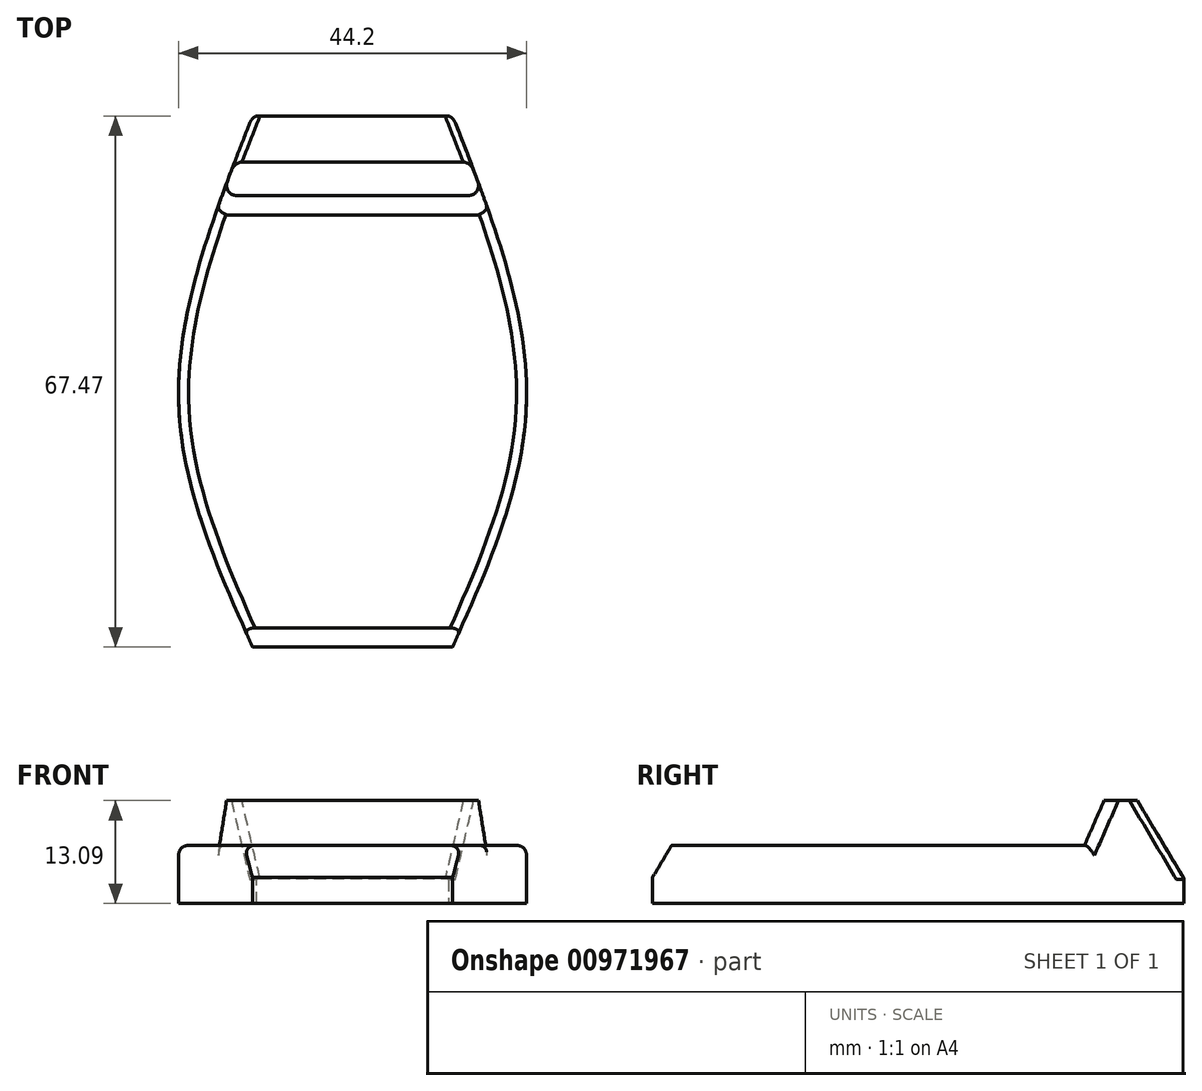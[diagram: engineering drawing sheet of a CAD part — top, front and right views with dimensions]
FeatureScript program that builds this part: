
annotation { "Feature Type Name" : "Feature", "Feature Type Description" : "" }
export const myFeature = defineFeature(function(context is Context, id is Id, definition is map)
    precondition{}
    {
        {
            var Q0;
            Q0=qCreatedBy(makeId("Right.planeOp"),FACE);
            var sketch = newSketch(context, id + "F0", { "sketchPlane" : qUnion([Q0])});
            skLineSegment(sketch, "E0", {"start": v(-30.67, 0) * mm, "end": v(37.07, 0) * mm});
            skLineSegment(sketch, "E1", {"start": v(-17.97, 4.35) * mm, "end": v(24.37, 4.35) * mm});
            skLineSegment(sketch, "E2", {"start": v(37.07, 0) * mm, "end": v(31.1, 10.04) * mm});
            skLineSegment(sketch, "E3", {"start": v(31.1, 10.04) * mm, "end": v(26.86, 10.04) * mm});
            skLineSegment(sketch, "E4", {"start": v(26.86, 10.04) * mm, "end": v(24.37, 4.35) * mm});
            skLineSegment(sketch, "E5", {"start": v(3.2, 0) * mm, "end": v(3.2, 4.35) * mm});
            skLineSegment(sketch, "E6.bottom", {"start": v(-67.15, 50) * mm, "end": v(95.4, 50) * mm});
            skLineSegment(sketch, "E6.top", {"start": v(-67.15, -41.02) * mm, "end": v(95.4, -41.02) * mm});
            skLineSegment(sketch, "E6.left", {"start": v(-67.15, 50) * mm, "end": v(-67.15, -41.02) * mm});
            skLineSegment(sketch, "E6.right", {"start": v(95.4, 50) * mm, "end": v(95.4, -41.02) * mm});
            skLineSegment(sketch, "E7", {"start": v(-17.97, 4.35) * mm, "end": v(-28.07, 4.35) * mm});
            skLineSegment(sketch, "E8", {"start": v(-28.07, 4.35) * mm, "end": v(-30.67, 0) * mm});
            skSolve(sketch);
        }
        {
            var Q0;
            Q0=qCreatedBy(makeId("Top.planeOp"),FACE);
            var sketch = newSketch(context, id + "F1", { "sketchPlane" : qUnion([Q0])});
            skLineSegment(sketch, "E9", {"start": v(0, 11.41) * mm, "end": v(0, -9.41) * mm});
            skLineSegment(sketch, "E10", {"start": v(0, 1) * mm, "end": v(-22.1, 1) * mm});
            skLineSegment(sketch, "E11", {"start": v(0, 1) * mm, "end": v(0, -30.51) * mm});
            skLineSegment(sketch, "E12", {"start": v(0, -30.51) * mm, "end": v(0, 36.96) * mm});
            skLineSegment(sketch, "E13", {"start": v(0, 36.96) * mm, "end": v(-12.7, 36.96) * mm});
            skLineSegment(sketch, "E14", {"start": v(0, 36.96) * mm, "end": v(12.7, 36.96) * mm});
            skLineSegment(sketch, "E15", {"start": v(0, -30.51) * mm, "end": v(-12.7, -30.51) * mm});
            skLineSegment(sketch, "E16", {"start": v(0, -30.51) * mm, "end": v(12.7, -30.51) * mm});
            skLineSegment(sketch, "E17", {"start": v(0, 1) * mm, "end": v(22.1, 1) * mm});
            skFitSpline(sketch, "E18", {"points": [v(-12.7, 36.96) * mm, v(-22.1, 1) * mm, v(-12.7, -30.51) * mm], "startDerivative": vector(-27.93, -71.02) * mm, "endDerivative": vector(28.5, -63.86) * mm});
            skFitSpline(sketch, "E19", {"points": [v(12.7, 36.96) * mm, v(22.1, 1) * mm, v(12.7, -30.51) * mm], "startDerivative": vector(27.93, -71.02) * mm, "endDerivative": vector(-28.5, -63.86) * mm});
            skSolve(sketch);
        }
        {
            var Q0;
            {var subQ1=sQuery(id+"F1.wireOp",EDGE,"E16");Q0=makeQuery(id+"F1.imprint","IMPRINT",FACE,{"disambiguationData":[TD([[makeQuery(id+"F1.imprint","IMPRINT",EDGE,{"derivedFrom":subQ1}),1.0]])]});}
            var Q1;
            {var subQ0=sQuery(id+"F1.wireOp",EDGE,"E14");Q1=makeQuery(id+"F1.imprint","IMPRINT",FACE,{"disambiguationData":[TD([[makeQuery(id+"F1.imprint","IMPRINT",EDGE,{"derivedFrom":subQ0}),-1.0]])]});}
            var Q2;
            {var subQ3=sQuery(id+"F1.wireOp",EDGE,"E10");Q2=makeQuery(id+"F1.imprint","IMPRINT",FACE,{"disambiguationData":[TD([[makeQuery(id+"F1.imprint","IMPRINT",EDGE,{"derivedFrom":subQ3}),-1.0]])]});}
            var Q3;
            {var subQ2=sQuery(id+"F1.wireOp",EDGE,"E10");Q3=makeQuery(id+"F1.imprint","IMPRINT",FACE,{"disambiguationData":[TD([[makeQuery(id+"F1.imprint","IMPRINT",EDGE,{"derivedFrom":subQ2}),1.0]])]});}
            extrude(context, id + "F2", {"entities" : qUnion([Q0, Q1, Q2, Q3]), "depth" : 10.04 * mm, "offsetDistance" : 25.4 * mm});
        }
        {
            var Q0;
            {var subQ9=sQuery(id+"F0.wireOp",EDGE,"f0UAfcan-YOLZ-XBiN-rJME-h1AG6BsoBLqj");Q0=makeQuery(id+"F0.imprint","IMPRINT",FACE,{"disambiguationData":[TD([[makeQuery(id+"F0.imprint","IMPRINT",EDGE,{"derivedFrom":subQ9}),-1.0]])]});}
            var Q1;
            {var subQ1=sQuery(id+"F0.wireOp",EDGE,"E2");Q1=makeQuery(id+"F0.imprint","IMPRINT",FACE,{"disambiguationData":[TD([[makeQuery(id+"F0.imprint","IMPRINT",EDGE,{"derivedFrom":subQ1}),-1.0]])]});}
            extrude(context, id + "F3", {"entities" : qUnion([Q0, Q1]), "operationType" : NewBodyOperationType.REMOVE, "endBound" : BoundingType.SYMMETRIC, "oppositeDirection" : true, "depth" : 73.15 * mm, "offsetDistance" : 25.4 * mm});
        }
        {
            var Q0;
            Q0=makeQuery(id+"F3.boolean.opBoolean","INTERSECT",EDGE,{"derivedFrom":[makeQuery(id+"F2.opExtrude","SWEPT_FACE",FACE,{"disambiguationData":[OSD([sQuery(id+"F1.wireOp",EDGE,"E18")])]}),makeQuery(id+"F3.opExtrude","SWEPT_FACE",FACE,{"disambiguationData":[OSD([sQuery(id+"F0.wireOp",EDGE,"E1")])]})]});
            var Q1;
            Q1=makeQuery(id+"F3.boolean.opBoolean","INTERSECT",EDGE,{"derivedFrom":[makeQuery(id+"F2.opExtrude","SWEPT_FACE",FACE,{"disambiguationData":[OSD([sQuery(id+"F1.wireOp",EDGE,"E18")])]}),makeQuery(id+"F3.opExtrude","SWEPT_FACE",FACE,{"disambiguationData":[OSD([sQuery(id+"F0.wireOp",EDGE,"E4")])]})]});
            var Q2;
            Q2=makeQuery(id+"F3.boolean.opBoolean","INTERSECT",EDGE,{"derivedFrom":[makeQuery(id+"F2.opExtrude","SWEPT_FACE",FACE,{"disambiguationData":[OSD([sQuery(id+"F1.wireOp",EDGE,"E19")])]}),makeQuery(id+"F3.opExtrude","SWEPT_FACE",FACE,{"disambiguationData":[OSD([sQuery(id+"F0.wireOp",EDGE,"E4")])]})]});
            var Q3;
            Q3=makeQuery(id+"F3.boolean.opBoolean","INTERSECT",EDGE,{"derivedFrom":[makeQuery(id+"F2.opExtrude","SWEPT_FACE",FACE,{"disambiguationData":[OSD([sQuery(id+"F1.wireOp",EDGE,"E19")])]}),makeQuery(id+"F3.opExtrude","SWEPT_FACE",FACE,{"disambiguationData":[OSD([sQuery(id+"F0.wireOp",EDGE,"E1")])]})]});
            var Q4;
            Q4=makeQuery(id+"F3.boolean.opBoolean","INTERSECT",EDGE,{"derivedFrom":[makeQuery(id+"F2.opExtrude","SWEPT_FACE",FACE,{"disambiguationData":[OSD([sQuery(id+"F1.wireOp",EDGE,"E19")])]}),makeQuery(id+"F3.opExtrude","SWEPT_FACE",FACE,{"disambiguationData":[OSD([sQuery(id+"F0.wireOp",EDGE,"5HqzP0p4-EUWS-5hlx-exL3-PoZeFwzppDlw")])]})]});
            var Q5;
            Q5=makeQuery(id+"F3.boolean.opBoolean","COPY",EDGE,{"derivedFrom":makeQuery(id+"F3.opExtrude","SWEPT_EDGE",EDGE,{"disambiguationData":[OSD([sQuery(id+"F0.wireOp",EDGE,"7wv0nnnK-TNmH-RVlH-PWxV-5QK5uFxknzdq"),sQuery(id+"F0.wireOp",EDGE,"5HqzP0p4-EUWS-5hlx-exL3-PoZeFwzppDlw")])]})});
            var Q6;
            Q6=makeQuery(id+"F3.boolean.opBoolean","INTERSECT",EDGE,{"derivedFrom":[makeQuery(id+"F2.opExtrude","SWEPT_FACE",FACE,{"disambiguationData":[OSD([sQuery(id+"F1.wireOp",EDGE,"E18")])]}),makeQuery(id+"F3.opExtrude","SWEPT_FACE",FACE,{"disambiguationData":[OSD([sQuery(id+"F0.wireOp",EDGE,"5HqzP0p4-EUWS-5hlx-exL3-PoZeFwzppDlw")])]})]});
            var Q7;
            Q7=makeQuery(id+"F3.boolean.opBoolean","INTERSECT",EDGE,{"derivedFrom":[makeQuery(id+"F2.opExtrude","SWEPT_FACE",FACE,{"disambiguationData":[OSD([sQuery(id+"F1.wireOp",EDGE,"E18")])]}),makeQuery(id+"F3.opExtrude","SWEPT_FACE",FACE,{"disambiguationData":[OSD([sQuery(id+"F0.wireOp",EDGE,"f0UAfcan-YOLZ-XBiN-rJME-h1AG6BsoBLqj")])]})]});
            var Q8;
            Q8=makeQuery(id+"F3.boolean.opBoolean","INTERSECT",EDGE,{"derivedFrom":[makeQuery(id+"F2.opExtrude","SWEPT_FACE",FACE,{"disambiguationData":[OSD([sQuery(id+"F1.wireOp",EDGE,"E19")])]}),makeQuery(id+"F3.opExtrude","SWEPT_FACE",FACE,{"disambiguationData":[OSD([sQuery(id+"F0.wireOp",EDGE,"f0UAfcan-YOLZ-XBiN-rJME-h1AG6BsoBLqj")])]})]});
            var Q9;
            Q9=makeQuery(id+"F3.boolean.opBoolean","COPY",EDGE,{"derivedFrom":makeQuery(id+"F3.opExtrude","SWEPT_EDGE",EDGE,{"disambiguationData":[OSD([sQuery(id+"F0.wireOp",EDGE,"f0UAfcan-YOLZ-XBiN-rJME-h1AG6BsoBLqj"),sQuery(id+"F0.wireOp",EDGE,"7wv0nnnK-TNmH-RVlH-PWxV-5QK5uFxknzdq")])]})});
            var Q10;
            Q10=makeQuery(id+"F3.boolean.opBoolean","INTERSECT",EDGE,{"derivedFrom":[makeQuery(id+"F2.opExtrude","SWEPT_FACE",FACE,{"disambiguationData":[OSD([sQuery(id+"F1.wireOp",EDGE,"E18")])]}),makeQuery(id+"F3.opExtrude","SWEPT_FACE",FACE,{"disambiguationData":[OSD([sQuery(id+"F0.wireOp",EDGE,"E2")])]})]});
            var Q11;
            Q11=makeQuery(id+"F3.boolean.opBoolean","INTERSECT",EDGE,{"derivedFrom":[makeQuery(id+"F2.opExtrude","SWEPT_FACE",FACE,{"disambiguationData":[OSD([sQuery(id+"F1.wireOp",EDGE,"E19")])]}),makeQuery(id+"F3.opExtrude","SWEPT_FACE",FACE,{"disambiguationData":[OSD([sQuery(id+"F0.wireOp",EDGE,"E2")])]})]});
            var Q12;
            Q12=makeQuery(id+"F3.boolean.opBoolean","COPY",EDGE,{"derivedFrom":makeQuery(id+"F3.opExtrude","SWEPT_EDGE",EDGE,{"disambiguationData":[OSD([sQuery(id+"F0.wireOp",EDGE,"E2"),sQuery(id+"F0.wireOp",EDGE,"E3")])]})});
            fillet(context, id + "F4", {"entities" : qUnion([Q0, Q1, Q2, Q3, Q4, Q5, Q6, Q7, Q8, Q9, Q10, Q11, Q12]), "radius" : 1.27 * mm, "tangentPropagation" : true, "allowEdgeOverflow" : false});
        }
        {
            var Q0;
            Q0=qCreatedBy(makeId("Front.planeOp"),FACE);
            var sketch = newSketch(context, id + "F5", { "sketchPlane" : qUnion([Q0])});
            skLineSegment(sketch, "E20", {"start": v(22.83, -0.17) * mm, "end": v(22.83, -11.6) * mm});
            skLineSegment(sketch, "E21", {"start": v(-22.9, -11.6) * mm, "end": v(-22.9, -0.17) * mm});
            skLineSegment(sketch, "E22", {"start": v(22.83, -5.89) * mm, "end": v(-22.9, -5.89) * mm});
            skArc(sketch, "E23", {"start": v(22.83, -11.6) * mm, "mid": v(-0.04, -8.1) * mm, "end": v(-22.9, -11.6) * mm});
            skArc(sketch, "E24", {"start": v(22.83, -0.17) * mm, "mid": v(-0.04, 3.34) * mm, "end": v(-22.9, -0.17) * mm});
            skSolve(sketch);
        }
        {
            var Q0;
            Q0=makeQuery(id+"F2.opExtrude","CAP_FACE",FACE,{"disambiguationData":[OSD([sQuery(id+"F1.wireOp",EDGE,"E13"),sQuery(id+"F1.wireOp",EDGE,"E14"),sQuery(id+"F1.wireOp",EDGE,"E15"),sQuery(id+"F1.wireOp",EDGE,"E16"),sQuery(id+"F1.wireOp",EDGE,"E18"),sQuery(id+"F1.wireOp",EDGE,"E19")])],"isStart":true});
            extrude(context, id + "F6", {"entities" : qUnion([Q0]), "operationType" : NewBodyOperationType.ADD, "depth" : 3.05 * mm, "offsetDistance" : 25.4 * mm});
        }
    });
